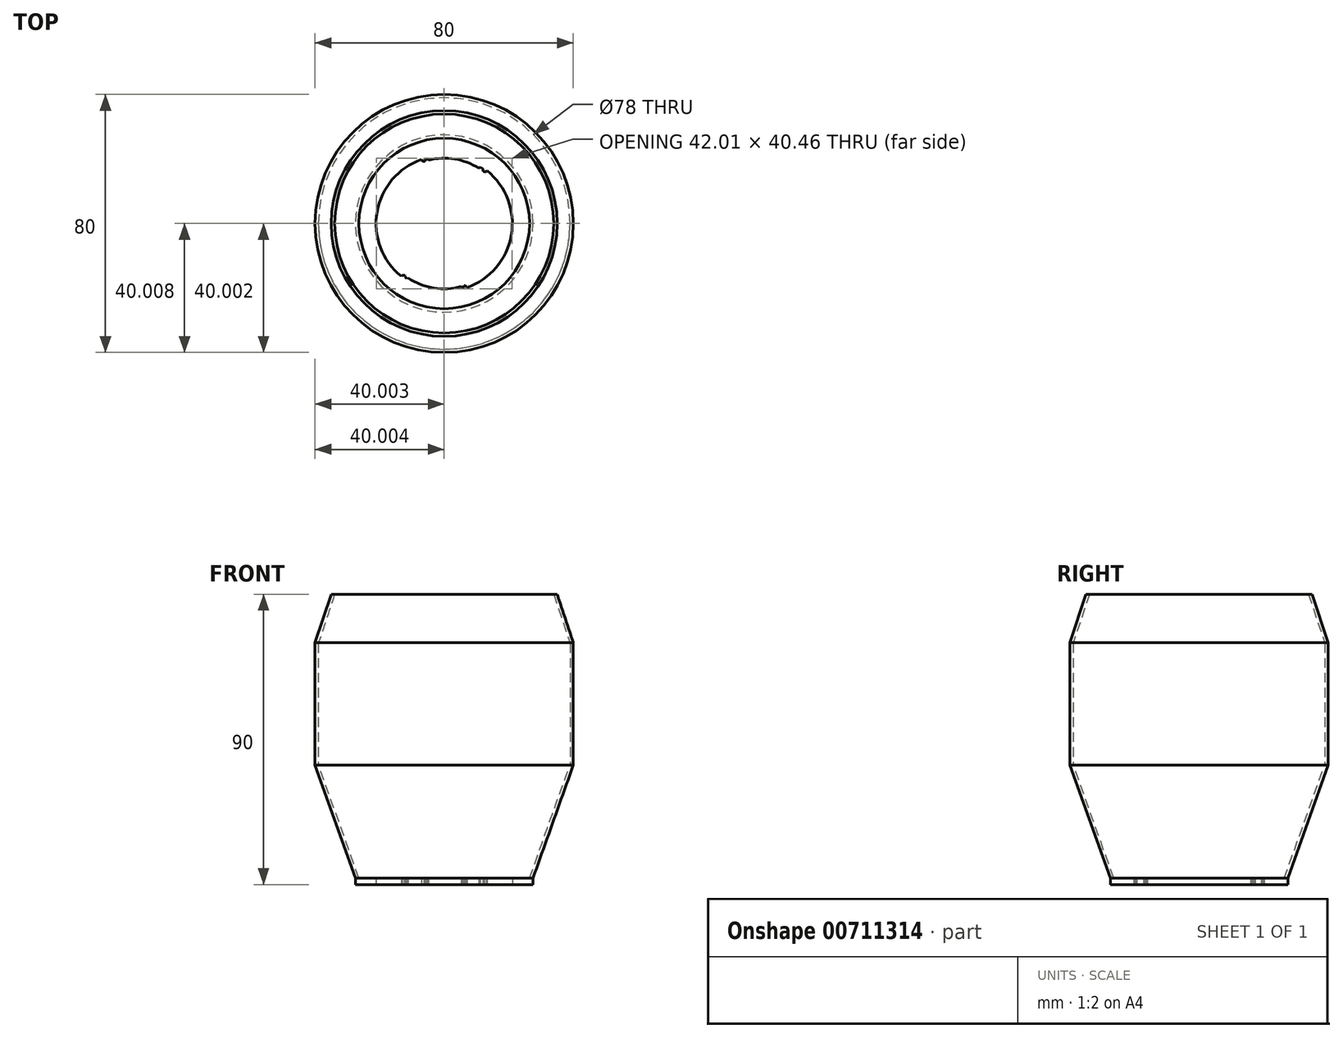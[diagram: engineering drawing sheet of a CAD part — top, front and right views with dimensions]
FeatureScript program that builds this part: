
annotation { "Feature Type Name" : "Feature", "Feature Type Description" : "" }
export const myFeature = defineFeature(function(context is Context, id is Id, definition is map)
    precondition{}
    {
        {
            var Q0;
            Q0=qCreatedBy(makeId("Top.planeOp"),FACE);
            var sketch = newSketch(context, id + "F0", { "sketchPlane" : qUnion([Q0])});
            skArc(sketch, "E0", {"start": v(-3.36, 18.49) * mm, "mid": v(-17.12, 2.18) * mm, "end": v(-9.62, -17.8) * mm});
            skArc(sketch, "E1", {"start": v(-9.08, -17.14) * mm, "mid": v(0.23, -21.36) * mm, "end": v(10.42, -20.5) * mm});
            skLineSegment(sketch, "E2", {"start": v(16.43, 14.32) * mm, "end": v(16.96, 14.98) * mm});
            skLineSegment(sketch, "E3.MirrorCS", {"start": v(-3.07, 17.68) * mm, "end": v(-3.36, 18.49) * mm});
            skLineSegment(sketch, "E4.MirrorCS", {"start": v(-9.08, -17.14) * mm, "end": v(-9.62, -17.8) * mm});
            skLineSegment(sketch, "E5.MirrorCS", {"start": v(10.42, -20.5) * mm, "end": v(10.7, -21.3) * mm});
            skArc(sketch, "E6.trimOffspring", {"start": v(10.7, -21.3) * mm, "mid": v(24.47, -5) * mm, "end": v(16.96, 14.98) * mm});
            skArc(sketch, "E7.trimOffspring", {"start": v(16.43, 14.32) * mm, "mid": v(7.12, 18.55) * mm, "end": v(-3.07, 17.68) * mm});
            skLineSegment(sketch, "E8", {"start": v(3.67, -1.4) * mm, "end": v(3.23, 23.59) * mm, "construction": true});
            skLineSegment(sketch, "E9.0", {"start": v(2.18, 17.53) * mm, "end": v(16.96, 14.98) * mm, "construction": true});
            skLineSegment(sketch, "E9.1", {"start": v(2.18, 17.53) * mm, "end": v(3.23, 23.59) * mm, "construction": true});
            skCircle(sketch, "E10", {"center": v(3.67, -1.4) * mm, "radius": 27.5 * mm});
            skSolve(sketch);
        }
        {
            var Q0;
            Q0 = qSketchRegion(id + "F0", true);
            extrude(context, id + "F1", {"entities" : qUnion([Q0]), "depth" : 2 * mm, "offsetDistance" : 25 * mm});
        }
        {
            var Q0;
            Q0=makeQuery(id+"F1.opExtrude","CAP_FACE",FACE,{"disambiguationData":[OSD([sQuery(id+"F0.wireOp",EDGE,"E0"),sQuery(id+"F0.wireOp",EDGE,"E1"),sQuery(id+"F0.wireOp",EDGE,"E2"),sQuery(id+"F0.wireOp",EDGE,"E3.MirrorCS"),sQuery(id+"F0.wireOp",EDGE,"E4.MirrorCS"),sQuery(id+"F0.wireOp",EDGE,"E5.MirrorCS"),sQuery(id+"F0.wireOp",EDGE,"E6.trimOffspring"),sQuery(id+"F0.wireOp",EDGE,"E7.trimOffspring"),sQuery(id+"F0.wireOp",EDGE,"E10")])],"isStart":false});
            var sketch = newSketch(context, id + "F2", { "sketchPlane" : qUnion([Q0])});
            skLineSegment(sketch, "E11", {"start": v(15.63, 14.21) * mm, "end": v(15.63, 15.58) * mm});
            skLineSegment(sketch, "E12", {"start": v(15.63, 15.58) * mm, "end": v(14.9, 16.06) * mm});
            skLineSegment(sketch, "E13", {"start": v(14.9, 16.06) * mm, "end": v(13.78, 15.27) * mm});
            skLineSegment(sketch, "E14", {"start": v(13.78, 15.27) * mm, "end": v(15.63, 14.21) * mm});
            skCircle(sketch, "E15.0", {"center": v(3.67, -1.4) * mm, "radius": 27.5 * mm, "construction": true});
            skLineSegment(sketch, "E16", {"start": v(-2.33, 17.34) * mm, "end": v(-2.11, 18.54) * mm});
            skLineSegment(sketch, "E17", {"start": v(-2.11, 18.54) * mm, "end": v(-1.56, 18.68) * mm});
            skLineSegment(sketch, "E18", {"start": v(-1.56, 18.68) * mm, "end": v(-0.62, 17.78) * mm});
            skLineSegment(sketch, "E19", {"start": v(-0.62, 17.78) * mm, "end": v(-2.25, 17.34) * mm});
            skLineSegment(sketch, "E20", {"start": v(-8.15, -16.76) * mm, "end": v(-8.47, -18.02) * mm});
            skLineSegment(sketch, "E21", {"start": v(-8.47, -18.02) * mm, "end": v(-7.96, -18.47) * mm});
            skLineSegment(sketch, "E22", {"start": v(-7.96, -18.47) * mm, "end": v(-6.82, -17.73) * mm});
            skLineSegment(sketch, "E23", {"start": v(-6.82, -17.73) * mm, "end": v(-8.15, -16.76) * mm});
            skLineSegment(sketch, "E24", {"start": v(9.84, -20) * mm, "end": v(9.73, -21.22) * mm});
            skLineSegment(sketch, "E25", {"start": v(9.73, -21.22) * mm, "end": v(9.3, -21.38) * mm});
            skLineSegment(sketch, "E26", {"start": v(9.3, -21.38) * mm, "end": v(8.47, -20.23) * mm});
            skLineSegment(sketch, "E27", {"start": v(8.47, -20.23) * mm, "end": v(9.84, -20) * mm});
            skSolve(sketch);
        }
        {
            var Q0;
            Q0 = qSketchRegion(id + "F2", true);
            var Q1;
            {var subQ0=sQuery(id+"F2.wireOp",EDGE,"E17");Q1=makeQuery(id+"F2.imprint","IMPRINT",FACE,{"disambiguationData":[TD([[makeQuery(id+"F2.imprint","IMPRINT",EDGE,{"derivedFrom":subQ0}),-1.0]])]});}
            extrude(context, id + "F3", {"entities" : qUnion([Q0, Q1]), "operationType" : NewBodyOperationType.REMOVE, "oppositeDirection" : true, "depth" : 25 * mm, "offsetDistance" : 25 * mm});
        }
        {
            var Q0;
            Q0=makeQuery(id+"F1.opExtrude","SWEPT_EDGE",EDGE,{"disambiguationData":[OSD([sQuery(id+"F0.wireOp",EDGE,"E3.MirrorCS"),sQuery(id+"F0.wireOp",EDGE,"E7.trimOffspring")])]});
            var Q1;
            Q1=makeQuery(id+"F1.opExtrude","SWEPT_EDGE",EDGE,{"disambiguationData":[OSD([sQuery(id+"F0.wireOp",EDGE,"E2"),sQuery(id+"F0.wireOp",EDGE,"E7.trimOffspring")])]});
            var Q2;
            Q2=makeQuery(id+"F1.opExtrude","SWEPT_EDGE",EDGE,{"disambiguationData":[OSD([sQuery(id+"F0.wireOp",EDGE,"E1"),sQuery(id+"F0.wireOp",EDGE,"E4.MirrorCS")])]});
            var Q3;
            Q3=makeQuery(id+"F1.opExtrude","SWEPT_EDGE",EDGE,{"disambiguationData":[OSD([sQuery(id+"F0.wireOp",EDGE,"E1"),sQuery(id+"F0.wireOp",EDGE,"E5.MirrorCS")])]});
            chamfer(context, id + "F4", {"entities" : qUnion([Q0, Q1, Q2, Q3]), "width" : 0.5 * mm, "tangentPropagation" : true});
        }
        {
            var Q0;
            Q0=makeQuery(id+"F1.opExtrude","CAP_FACE",FACE,{"disambiguationData":[OSD([sQuery(id+"F0.wireOp",EDGE,"E0"),sQuery(id+"F0.wireOp",EDGE,"E1"),sQuery(id+"F0.wireOp",EDGE,"E2"),sQuery(id+"F0.wireOp",EDGE,"E3.MirrorCS"),sQuery(id+"F0.wireOp",EDGE,"E4.MirrorCS"),sQuery(id+"F0.wireOp",EDGE,"E5.MirrorCS"),sQuery(id+"F0.wireOp",EDGE,"E6.trimOffspring"),sQuery(id+"F0.wireOp",EDGE,"E7.trimOffspring"),sQuery(id+"F0.wireOp",EDGE,"E10")])],"isStart":false});
            var sketch = newSketch(context, id + "F5", { "sketchPlane" : qUnion([Q0])});
            skCircle(sketch, "E28.0", {"center": v(3.67, -1.4) * mm, "radius": 27.5 * mm, "construction": true});
            skCircle(sketch, "E29", {"center": v(3.67, -1.4) * mm, "radius": 40 * mm});
            skSolve(sketch);
        }
        {
            var Q0;
            Q0 = qSketchRegion(id + "F5", true);
            extrude(context, id + "F6", {"entities" : qUnion([Q0]), "depth" : 88 * mm, "offsetDistance" : 25 * mm});
        }
        {
            var Q0;
            Q0=makeQuery(id+"F6.opExtrude","CAP_EDGE",EDGE,{"disambiguationData":[OSD([sQuery(id+"F5.wireOp",EDGE,"E29")])],"isStart":false});
            chamfer(context, id + "F7", {"entities" : qUnion([Q0]), "chamferType" : ChamferType.TWO_OFFSETS, "width1" : 5 * mm, "oppositeDirection" : false, "width2" : 15 * mm, "tangentPropagation" : true});
        }
        {
            var Q0;
            Q0=makeQuery(id+"F6.opExtrude","CAP_EDGE",EDGE,{"disambiguationData":[OSD([sQuery(id+"F5.wireOp",EDGE,"E29")])],"isStart":true});
            chamfer(context, id + "F8", {"entities" : qUnion([Q0]), "chamferType" : ChamferType.TWO_OFFSETS, "width1" : 35 * mm, "oppositeDirection" : false, "width2" : 12.5 * mm, "tangentPropagation" : true});
        }
        {
            var Q0;
            Q0=makeQuery(id+"F6.opExtrude","CAP_FACE",FACE,{"disambiguationData":[OSD([sQuery(id+"F5.wireOp",EDGE,"E29")])],"isStart":true});
            var Q1;
            Q1=makeQuery(id+"F6.opExtrude","CAP_FACE",FACE,{"disambiguationData":[OSD([sQuery(id+"F5.wireOp",EDGE,"E29")])],"isStart":false});
            shell(context, id + "F9", {"entities" : qUnion([Q0, Q1]), "thickness" : 1 * mm});
        }
    });
